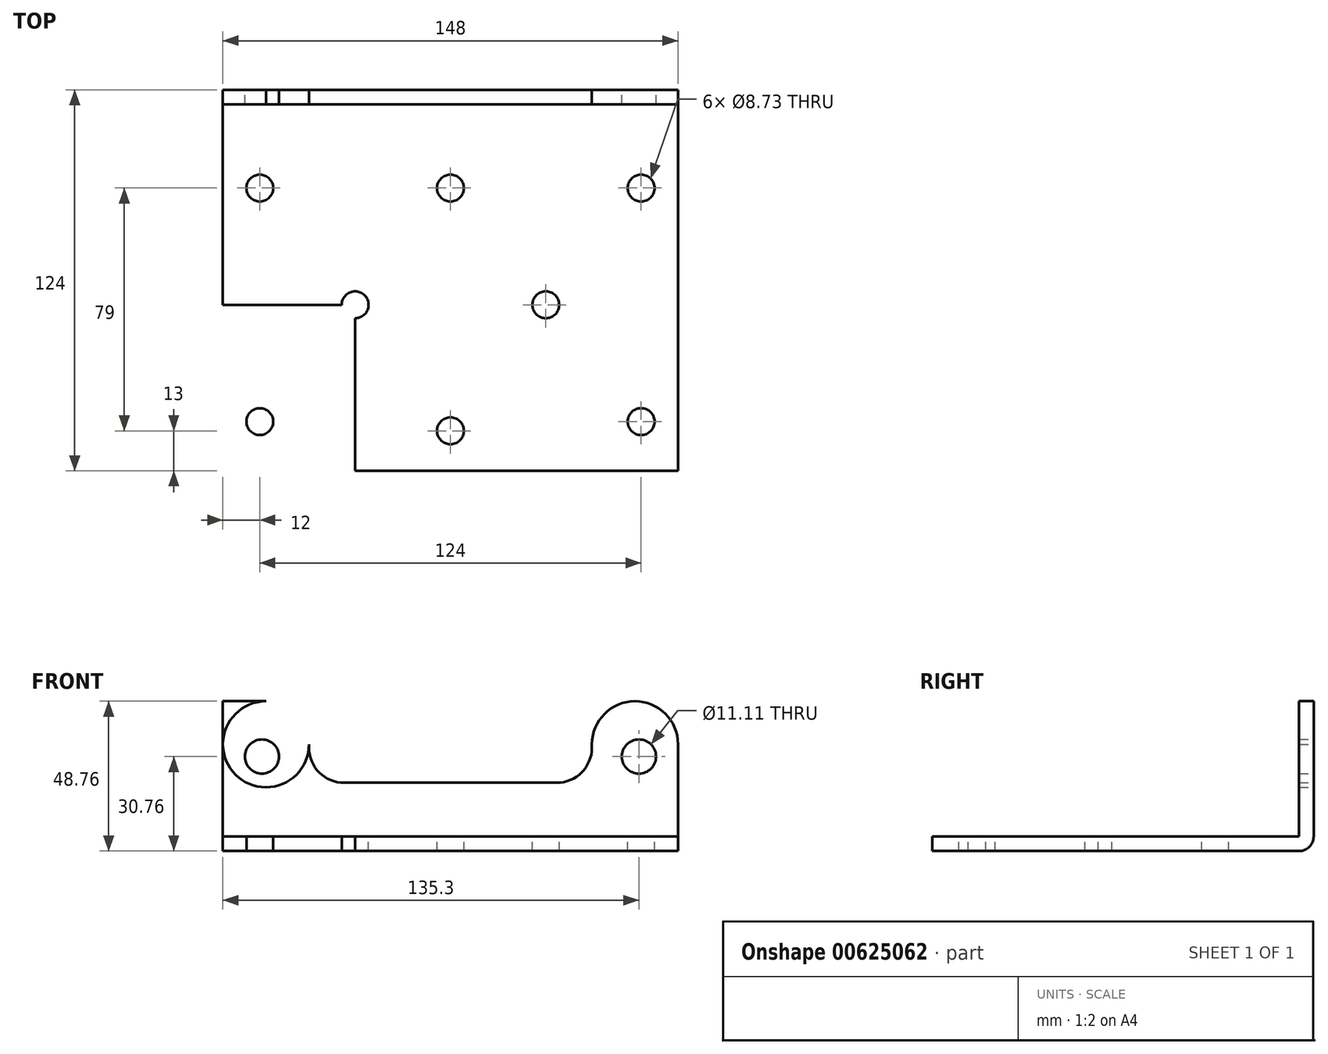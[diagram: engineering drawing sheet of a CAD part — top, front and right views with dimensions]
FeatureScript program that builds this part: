
annotation { "Feature Type Name" : "Feature", "Feature Type Description" : "" }
export const myFeature = defineFeature(function(context is Context, id is Id, definition is map)
    precondition{}
    {
        {
            var Q0;
            Q0=qCreatedBy(makeId("Top.planeOp"),FACE);
            var sketch = newSketch(context, id + "F0", { "sketchPlane" : qUnion([Q0])});
            skLineSegment(sketch, "E0.bottom", {"start": v(-74, -62) * mm, "end": v(74, -62) * mm});
            skLineSegment(sketch, "E0.top", {"start": v(-74, 62) * mm, "end": v(74, 62) * mm});
            skLineSegment(sketch, "E0.left", {"start": v(-74, -62) * mm, "end": v(-74, 62) * mm});
            skLineSegment(sketch, "E0.right", {"start": v(74, -62) * mm, "end": v(74, 62) * mm});
            skPoint(sketch, "E0.middle", {"position": v(0, 0) * mm});
            skLineSegment(sketch, "E1.top", {"start": v(-74, 57.24) * mm, "end": v(74, 57.24) * mm});
            skLineSegment(sketch, "E1.left", {"start": v(-74, 62) * mm, "end": v(-74, 57.24) * mm});
            skLineSegment(sketch, "E1.right", {"start": v(74, 62) * mm, "end": v(74, 57.24) * mm});
            skLineSegment(sketch, "E2", {"start": v(0, -62) * mm, "end": v(0, -49) * mm});
            skLineSegment(sketch, "E3", {"start": v(0, -49) * mm, "end": v(0, 30) * mm});
            skCircle(sketch, "E4", {"center": v(0, 30) * mm, "radius": 4.37 * mm});
            skCircle(sketch, "E5", {"center": v(0, -49) * mm, "radius": 4.37 * mm});
            skLineSegment(sketch, "E6.bottom", {"start": v(-74, -62) * mm, "end": v(-62, -62) * mm});
            skLineSegment(sketch, "E6.top", {"start": v(-74, -46) * mm, "end": v(-62, -46) * mm});
            skLineSegment(sketch, "E6.left", {"start": v(-74, -62) * mm, "end": v(-74, -46) * mm});
            skLineSegment(sketch, "E6.right", {"start": v(-62, -62) * mm, "end": v(-62, -46) * mm});
            skCircle(sketch, "E7", {"center": v(-62, -46) * mm, "radius": 4.37 * mm});
            skLineSegment(sketch, "E8", {"start": v(-62, -46) * mm, "end": v(-62, 30) * mm});
            skCircle(sketch, "E9", {"center": v(-62, 30) * mm, "radius": 4.37 * mm});
            skLineSegment(sketch, "E10.bottom", {"start": v(-74, -62) * mm, "end": v(-31, -62) * mm});
            skLineSegment(sketch, "E10.top", {"start": v(-74, -8) * mm, "end": v(-31, -8) * mm});
            skLineSegment(sketch, "E10.left", {"start": v(-74, -62) * mm, "end": v(-74, -8) * mm});
            skLineSegment(sketch, "E10.right", {"start": v(-31, -62) * mm, "end": v(-31, -8) * mm});
            skCircle(sketch, "E11", {"center": v(-31, -8) * mm, "radius": 4.37 * mm});
            skCircle(sketch, "E12.MirrorC", {"center": v(62, 30) * mm, "radius": 4.37 * mm});
            skCircle(sketch, "E13.MirrorC", {"center": v(31, -8) * mm, "radius": 4.37 * mm});
            skCircle(sketch, "E14.MirrorC", {"center": v(62, -46) * mm, "radius": 4.37 * mm});
            skSolve(sketch);
        }
        {
            var Q0;
            Q0=makeQuery(id+"F0.imprint","IMPRINT",FACE,{"disambiguationData":[TD([[makeQuery(id+"F0.imprint","IMPRINT",EDGE,{"derivedFrom":sQuery(id+"F0.wireOp",EDGE,"E0.bottom")}),1.0]])]});
            var Q1;
            Q1=makeQuery(id+"F0.imprint","IMPRINT",FACE,{"disambiguationData":[TD([[makeQuery(id+"F0.imprint","IMPRINT",EDGE,{"derivedFrom":sQuery(id+"F0.wireOp",EDGE,"E0.top")}),-1.0]])]});
            var Q2;
            {var subQ9=sQuery(id+"F0.wireOp",EDGE,"E10.bottom");var subQ11=sQuery(id+"F0.wireOp",EDGE,"E6.right");var subQ12=makeQuery(id+"F0.imprint","INTERSECT",VERTEX,{"derivedFrom":[subQ11,subQ9]});Q2=makeQuery(id+"F0.imprint","IMPRINT",FACE,{"disambiguationData":[TD([[makeQuery(id+"F0.imprint","IMPRINT",EDGE,{"disambiguationData":[TD([[subQ12,-1.0]])],"derivedFrom":subQ11}),-1.0]])]});}
            var Q3;
            {var subQ0=sQuery(id+"F0.wireOp",EDGE,"E10.left");var subQ7=sQuery(id+"F0.wireOp",EDGE,"E6.top");var subQ9=makeQuery(id+"F0.imprint","INTERSECT",VERTEX,{"derivedFrom":[subQ7,subQ0]});Q3=makeQuery(id+"F0.imprint","IMPRINT",FACE,{"disambiguationData":[TD([[makeQuery(id+"F0.imprint","IMPRINT",EDGE,{"disambiguationData":[TD([[subQ9,-1.0]])],"derivedFrom":subQ7}),1.0]])]});}
            var Q4;
            {var subQ5=sQuery(id+"F0.wireOp",EDGE,"E10.left");var subQ7=sQuery(id+"F0.wireOp",EDGE,"E6.top");var subQ9=makeQuery(id+"F0.imprint","INTERSECT",VERTEX,{"derivedFrom":[subQ7,subQ5]});Q4=makeQuery(id+"F0.imprint","IMPRINT",FACE,{"disambiguationData":[TD([[makeQuery(id+"F0.imprint","IMPRINT",EDGE,{"disambiguationData":[TD([[subQ9,-1.0]])],"derivedFrom":subQ7}),-1.0]])]});}
            extrude(context, id + "F1", {"entities" : qUnion([Q0, Q1, Q2, Q3, Q4]), "oppositeDirection" : true, "depth" : 4.76 * mm, "offsetDistance" : 25.4 * mm});
        }
        {
            var Q0;
            Q0=makeQuery(id+"F0.imprint","IMPRINT",FACE,{"disambiguationData":[TD([[makeQuery(id+"F0.imprint","IMPRINT",EDGE,{"derivedFrom":sQuery(id+"F0.wireOp",EDGE,"E0.top")}),-1.0]])]});
            extrude(context, id + "F2", {"entities" : qUnion([Q0]), "operationType" : NewBodyOperationType.ADD, "depth" : 44 * mm, "offsetDistance" : 25.4 * mm});
        }
        {
            var Q0;
            Q0=makeQuery(id+"F1.opExtrude","CAP_EDGE",EDGE,{"disambiguationData":[OSD([sQuery(id+"F0.wireOp",EDGE,"E0.top")])],"isStart":false});
            fillet(context, id + "F3", {"entities" : qUnion([Q0]), "radius" : 4.76 * mm, "tangentPropagation" : true, "allowEdgeOverflow" : false});
        }
        {
            var Q0;
            {var subQ0=sQuery(id+"F0.wireOp",EDGE,"E0.top");Q0=makeQuery(id+"F2.boolean.opBoolean","MERGE",FACE,{"derivedFrom":[makeQuery(id+"F1.opExtrude","SWEPT_FACE",FACE,{"disambiguationData":[OSD([subQ0])]}),makeQuery(id+"F2.opExtrude","SWEPT_FACE",FACE,{"disambiguationData":[OSD([subQ0])]})]});}
            var sketch = newSketch(context, id + "F4", { "sketchPlane" : qUnion([Q0])});
            skCircle(sketch, "E15", {"center": v(-60, 30) * mm, "radius": 14 * mm});
            skCircle(sketch, "E16", {"center": v(-61.3, 26) * mm, "radius": 5.56 * mm});
            skLineSegment(sketch, "E17", {"start": v(-74, 44) * mm, "end": v(-74, 30) * mm});
            skLineSegment(sketch, "E18", {"start": v(-46, 30) * mm, "end": v(-46, 28.9) * mm});
            skArc(sketch, "E19.filletArc", {"start": v(-46, 28.9) * mm, "mid": v(-42.65, 20.81) * mm, "end": v(-34.57, 17.46) * mm});
            skLineSegment(sketch, "E20", {"start": v(-34.57, 17.46) * mm, "end": v(0, 17.46) * mm});
            skLineSegment(sketch, "E21.MirrorCS", {"start": v(34.57, 17.46) * mm, "end": v(0, 17.46) * mm});
            skArc(sketch, "E22.MirrorCS", {"start": v(46, 28.9) * mm, "mid": v(42.65, 20.81) * mm, "end": v(34.57, 17.46) * mm});
            skCircle(sketch, "E23.MirrorC", {"center": v(60, 30) * mm, "radius": 14 * mm});
            skCircle(sketch, "E24.MirrorC", {"center": v(61.3, 26) * mm, "radius": 5.56 * mm});
            skLineSegment(sketch, "E25.MirrorCS", {"start": v(74, 44) * mm, "end": v(74, 30) * mm});
            skLineSegment(sketch, "E26.MirrorCS", {"start": v(74, 44) * mm, "end": v(59.71, 44) * mm});
            skLineSegment(sketch, "E27.MirrorCS", {"start": v(46, 30) * mm, "end": v(46, 28.9) * mm});
            skLineSegment(sketch, "E28", {"start": v(-60, 44) * mm, "end": v(-74, 44) * mm});
            skSolve(sketch);
        }
        {
            var Q0;
            {var subQ3=sQuery(id+"F4.wireOp",EDGE,"E18");Q0=makeQuery(id+"F4.imprint","IMPRINT",FACE,{"disambiguationData":[TD([[makeQuery(id+"F4.imprint","IMPRINT",EDGE,{"derivedFrom":subQ3}),1.0]])]});}
            var Q1;
            {var subQ0=sQuery(id+"F4.wireOp",EDGE,"D6uFYzgD-nF0j-uRRQ-kK9z-LAaavTDBkLQc");var subQ1=sQuery(id+"F4.wireOp",EDGE,"E15");var subQ2=makeQuery(id+"F4.imprint","INTERSECT",VERTEX,{"derivedFrom":[subQ1,subQ0]});Q1=makeQuery(id+"F4.imprint","IMPRINT",FACE,{"disambiguationData":[TD([[makeQuery(id+"F4.imprint","IMPRINT",EDGE,{"disambiguationData":[TD([[subQ2,-1.0]])],"derivedFrom":subQ1}),-1.0]])]});}
            var Q2;
            {var subQ0=sQuery(id+"F4.wireOp",EDGE,"E26.MirrorCS");var subQ1=sQuery(id+"F4.wireOp",EDGE,"E23.MirrorC");var subQ2=makeQuery(id+"F4.imprint","INTERSECT",VERTEX,{"derivedFrom":[subQ1,subQ0]});Q2=makeQuery(id+"F4.imprint","IMPRINT",FACE,{"disambiguationData":[TD([[makeQuery(id+"F4.imprint","IMPRINT",EDGE,{"disambiguationData":[TD([[subQ2,-1.0]])],"derivedFrom":subQ1}),1.0]])]});}
            var Q3;
            Q3=makeQuery(id+"F4.imprint","IMPRINT",FACE,{"disambiguationData":[TD([[makeQuery(id+"F4.imprint","IMPRINT",EDGE,{"derivedFrom":sQuery(id+"F4.wireOp",EDGE,"E16")}),1.0]])]});
            var Q4;
            Q4=makeQuery(id+"F4.imprint","IMPRINT",FACE,{"disambiguationData":[TD([[makeQuery(id+"F4.imprint","IMPRINT",EDGE,{"derivedFrom":sQuery(id+"F4.wireOp",EDGE,"E24.MirrorC")}),-1.0]])]});
            var Q5;
            {var subQ0=sQuery(id+"F4.wireOp",EDGE,"E17");Q5=makeQuery(id+"F4.imprint","IMPRINT",FACE,{"disambiguationData":[TD([[makeQuery(id+"F4.imprint","IMPRINT",EDGE,{"derivedFrom":subQ0}),-1.0]])]});}
            extrude(context, id + "F5", {"entities" : qUnion([Q0, Q1, Q2, Q3, Q4, Q5]), "operationType" : NewBodyOperationType.REMOVE, "oppositeDirection" : true, "depth" : 6.35 * mm, "offsetDistance" : 25.4 * mm});
        }
    });
